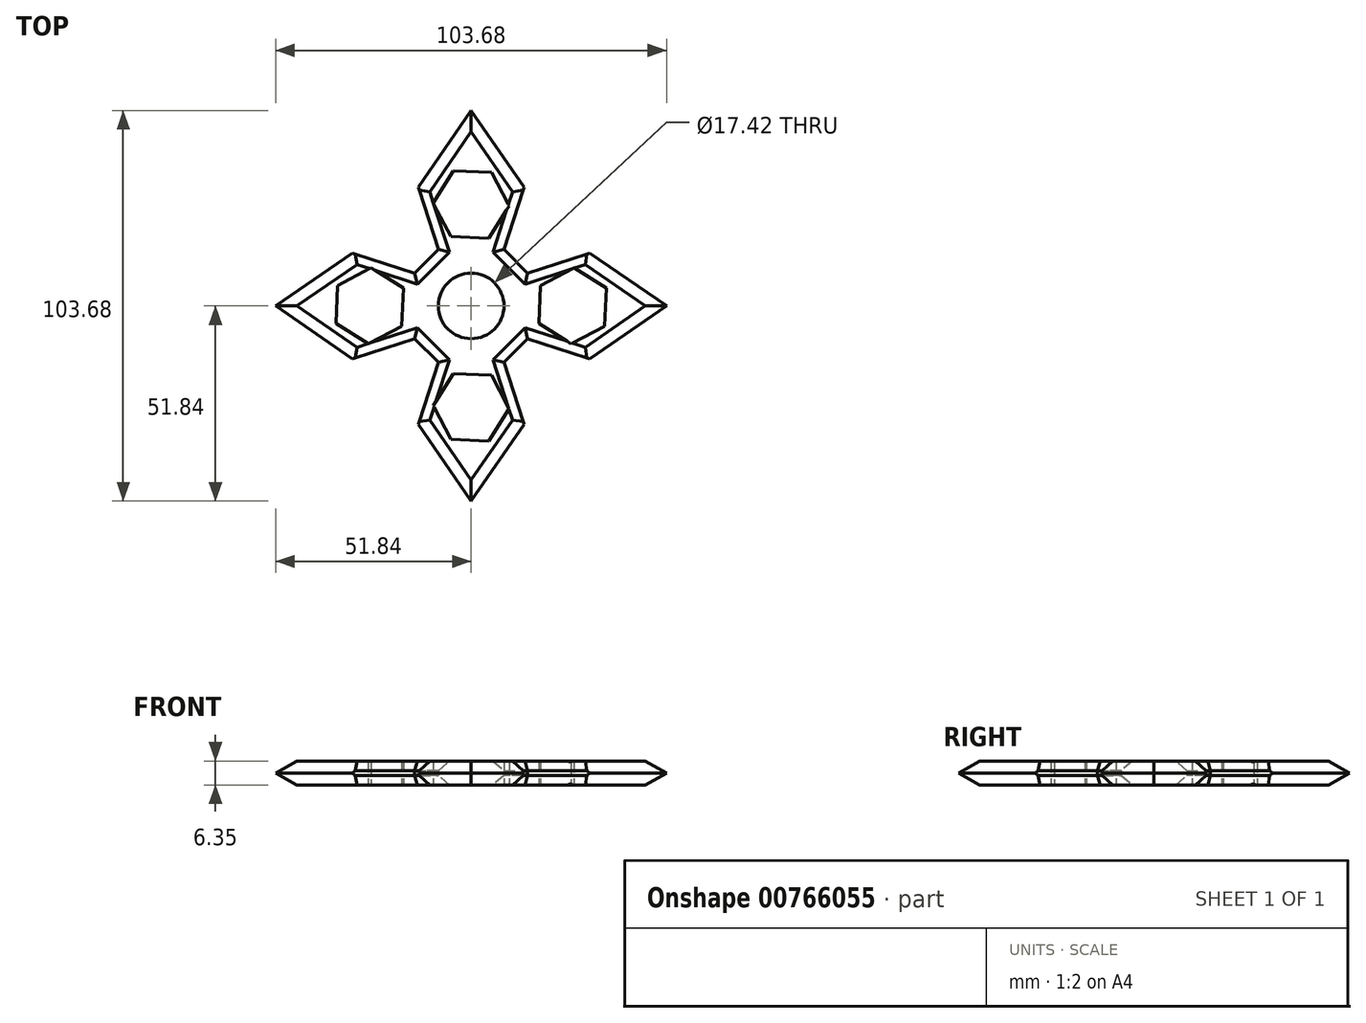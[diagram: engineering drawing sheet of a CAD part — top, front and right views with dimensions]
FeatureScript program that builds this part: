
annotation { "Feature Type Name" : "Feature", "Feature Type Description" : "" }
export const myFeature = defineFeature(function(context is Context, id is Id, definition is map)
    precondition{}
    {
        {
            var Q0;
            Q0=qCreatedBy(makeId("Top.planeOp"),FACE);
            var sketch = newSketch(context, id + "F0", { "sketchPlane" : qUnion([Q0])});
            skCircle(sketch, "E0", {"center": v(0, 0) * mm, "radius": 8.71 * mm});
            skCircle(sketch, "E1", {"center": v(0, 0) * mm, "radius": 14.29 * mm});
            skCircle(sketch, "E2.cCircle", {"center": v(0, 26.92) * mm, "radius": 8.73 * mm, "construction": true});
            skLineSegment(sketch, "E2.0", {"start": v(10.07, 26.52) * mm, "end": v(4.7, 18) * mm});
            skLineSegment(sketch, "E2.1", {"start": v(4.7, 18) * mm, "end": v(-5.38, 18.4) * mm});
            skLineSegment(sketch, "E2.2", {"start": v(-5.38, 18.4) * mm, "end": v(-10.07, 27.32) * mm});
            skLineSegment(sketch, "E2.3", {"start": v(-10.07, 27.32) * mm, "end": v(-4.7, 35.85) * mm});
            skLineSegment(sketch, "E2.4", {"start": v(-4.7, 35.85) * mm, "end": v(5.38, 35.45) * mm});
            skLineSegment(sketch, "E2.5", {"start": v(5.38, 35.45) * mm, "end": v(10.07, 26.52) * mm});
            skPoint(sketch, "E2.0.midPoint", {"position": v(7.38, 22.26) * mm});
            skCircle(sketch, "E3.cCircle", {"center": v(0, 26.92) * mm, "radius": 11.94 * mm, "construction": true});
            skLineSegment(sketch, "E3.0", {"start": v(8.67, 14.99) * mm, "end": v(-8.67, 14.99) * mm});
            skLineSegment(sketch, "E3.1", {"start": v(-8.67, 14.99) * mm, "end": v(-14.03, 31.48) * mm});
            skLineSegment(sketch, "E3.2", {"start": v(-14.03, 31.48) * mm, "end": v(0, 41.68) * mm});
            skLineSegment(sketch, "E3.3", {"start": v(0, 41.68) * mm, "end": v(14.03, 31.48) * mm});
            skLineSegment(sketch, "E3.4", {"start": v(14.03, 31.48) * mm, "end": v(8.67, 14.99) * mm});
            skPoint(sketch, "E3.0.midPoint", {"position": v(0, 14.99) * mm});
            skLineSegment(sketch, "E4", {"start": v(-14.03, 31.48) * mm, "end": v(0, 51.84) * mm});
            skLineSegment(sketch, "E5", {"start": v(0, 51.84) * mm, "end": v(14.03, 31.48) * mm});
            skPoint(sketch, "E6.1.0", {"position": v(-22.26, 7.38) * mm});
            skCircle(sketch, "E6.1.1", {"center": v(-26.92, 0) * mm, "radius": 8.73 * mm, "construction": true});
            skLineSegment(sketch, "E6.1.2", {"start": v(-14.99, 8.67) * mm, "end": v(-14.99, -8.67) * mm});
            skCircle(sketch, "E6.1.3", {"center": v(-26.92, 0) * mm, "radius": 11.94 * mm, "construction": true});
            skLineSegment(sketch, "E6.1.4", {"start": v(-35.45, 5.38) * mm, "end": v(-26.52, 10.07) * mm});
            skLineSegment(sketch, "E6.1.5", {"start": v(-41.68, 0) * mm, "end": v(-31.48, 14.03) * mm});
            skLineSegment(sketch, "E6.1.6", {"start": v(-31.48, -14.03) * mm, "end": v(-41.68, 0) * mm});
            skLineSegment(sketch, "E6.1.7", {"start": v(-31.48, 14.03) * mm, "end": v(-14.99, 8.67) * mm});
            skPoint(sketch, "E6.1.8", {"position": v(-14.99, 0) * mm});
            skLineSegment(sketch, "E6.1.9", {"start": v(-31.48, -14.03) * mm, "end": v(-51.84, 0) * mm});
            skLineSegment(sketch, "E6.1.10", {"start": v(-14.99, -8.67) * mm, "end": v(-31.48, -14.03) * mm});
            skLineSegment(sketch, "E6.1.11", {"start": v(-51.84, 0) * mm, "end": v(-31.48, 14.03) * mm});
            skLineSegment(sketch, "E6.1.12", {"start": v(-18.4, -5.38) * mm, "end": v(-27.32, -10.07) * mm});
            skLineSegment(sketch, "E6.1.13", {"start": v(-27.32, -10.07) * mm, "end": v(-35.85, -4.7) * mm});
            skLineSegment(sketch, "E6.1.14", {"start": v(-35.85, -4.7) * mm, "end": v(-35.45, 5.38) * mm});
            skLineSegment(sketch, "E6.1.15", {"start": v(-18, 4.7) * mm, "end": v(-18.4, -5.38) * mm});
            skLineSegment(sketch, "E6.1.16", {"start": v(-26.52, 10.07) * mm, "end": v(-18, 4.7) * mm});
            skPoint(sketch, "E6.2.0", {"position": v(-7.38, -22.26) * mm});
            skCircle(sketch, "E6.2.1", {"center": v(0, -26.92) * mm, "radius": 8.73 * mm, "construction": true});
            skLineSegment(sketch, "E6.2.2", {"start": v(-8.67, -14.99) * mm, "end": v(8.67, -14.99) * mm});
            skCircle(sketch, "E6.2.3", {"center": v(0, -26.92) * mm, "radius": 11.94 * mm, "construction": true});
            skLineSegment(sketch, "E6.2.4", {"start": v(-5.38, -35.45) * mm, "end": v(-10.07, -26.52) * mm});
            skLineSegment(sketch, "E6.2.5", {"start": v(0, -41.68) * mm, "end": v(-14.03, -31.48) * mm});
            skLineSegment(sketch, "E6.2.6", {"start": v(14.03, -31.48) * mm, "end": v(0, -41.68) * mm});
            skLineSegment(sketch, "E6.2.7", {"start": v(-14.03, -31.48) * mm, "end": v(-8.67, -14.99) * mm});
            skPoint(sketch, "E6.2.8", {"position": v(0, -14.99) * mm});
            skLineSegment(sketch, "E6.2.9", {"start": v(14.03, -31.48) * mm, "end": v(0, -51.84) * mm});
            skLineSegment(sketch, "E6.2.10", {"start": v(8.67, -14.99) * mm, "end": v(14.03, -31.48) * mm});
            skLineSegment(sketch, "E6.2.11", {"start": v(0, -51.84) * mm, "end": v(-14.03, -31.48) * mm});
            skLineSegment(sketch, "E6.2.12", {"start": v(5.38, -18.4) * mm, "end": v(10.07, -27.32) * mm});
            skLineSegment(sketch, "E6.2.13", {"start": v(10.07, -27.32) * mm, "end": v(4.7, -35.85) * mm});
            skLineSegment(sketch, "E6.2.14", {"start": v(4.7, -35.85) * mm, "end": v(-5.38, -35.45) * mm});
            skLineSegment(sketch, "E6.2.15", {"start": v(-4.7, -18) * mm, "end": v(5.38, -18.4) * mm});
            skLineSegment(sketch, "E6.2.16", {"start": v(-10.07, -26.52) * mm, "end": v(-4.7, -18) * mm});
            skPoint(sketch, "E6.3.0", {"position": v(22.26, -7.38) * mm});
            skCircle(sketch, "E6.3.1", {"center": v(26.92, 0) * mm, "radius": 8.73 * mm, "construction": true});
            skLineSegment(sketch, "E6.3.2", {"start": v(14.99, -8.67) * mm, "end": v(14.99, 8.67) * mm});
            skCircle(sketch, "E6.3.3", {"center": v(26.92, 0) * mm, "radius": 11.94 * mm, "construction": true});
            skLineSegment(sketch, "E6.3.4", {"start": v(35.45, -5.38) * mm, "end": v(26.52, -10.07) * mm});
            skLineSegment(sketch, "E6.3.5", {"start": v(41.68, 0) * mm, "end": v(31.48, -14.03) * mm});
            skLineSegment(sketch, "E6.3.6", {"start": v(31.48, 14.03) * mm, "end": v(41.68, 0) * mm});
            skLineSegment(sketch, "E6.3.7", {"start": v(31.48, -14.03) * mm, "end": v(14.99, -8.67) * mm});
            skPoint(sketch, "E6.3.8", {"position": v(14.99, 0) * mm});
            skLineSegment(sketch, "E6.3.9", {"start": v(31.48, 14.03) * mm, "end": v(51.84, 0) * mm});
            skLineSegment(sketch, "E6.3.10", {"start": v(14.99, 8.67) * mm, "end": v(31.48, 14.03) * mm});
            skLineSegment(sketch, "E6.3.11", {"start": v(51.84, 0) * mm, "end": v(31.48, -14.03) * mm});
            skLineSegment(sketch, "E6.3.12", {"start": v(18.4, 5.38) * mm, "end": v(27.32, 10.07) * mm});
            skLineSegment(sketch, "E6.3.13", {"start": v(27.32, 10.07) * mm, "end": v(35.85, 4.7) * mm});
            skLineSegment(sketch, "E6.3.14", {"start": v(35.85, 4.7) * mm, "end": v(35.45, -5.38) * mm});
            skLineSegment(sketch, "E6.3.15", {"start": v(18, -4.7) * mm, "end": v(18.4, 5.38) * mm});
            skLineSegment(sketch, "E6.3.16", {"start": v(26.52, -10.07) * mm, "end": v(18, -4.7) * mm});
            skLineSegment(sketch, "E7", {"start": v(-8.67, 14.99) * mm, "end": v(-14.99, 8.67) * mm});
            skLineSegment(sketch, "E8", {"start": v(-14.99, -8.67) * mm, "end": v(-8.67, -14.99) * mm});
            skLineSegment(sketch, "E9", {"start": v(8.67, -14.99) * mm, "end": v(14.99, -8.67) * mm});
            skLineSegment(sketch, "E10", {"start": v(14.99, 8.67) * mm, "end": v(8.67, 14.99) * mm});
            skSolve(sketch);
        }
        {
            var Q0;
            Q0=makeQuery(id+"F0.imprint","IMPRINT",FACE,{"disambiguationData":[TD([[makeQuery(id+"F0.imprint","IMPRINT",EDGE,{"derivedFrom":sQuery(id+"F0.wireOp",EDGE,"E6.1.5")}),1.0]])]});
            var Q1;
            Q1=makeQuery(id+"F0.imprint","IMPRINT",FACE,{"disambiguationData":[TD([[makeQuery(id+"F0.imprint","IMPRINT",EDGE,{"derivedFrom":sQuery(id+"F0.wireOp",EDGE,"E6.1.2")}),-1.0]])]});
            var Q2;
            Q2=makeQuery(id+"F0.imprint","IMPRINT",FACE,{"disambiguationData":[TD([[makeQuery(id+"F0.imprint","IMPRINT",EDGE,{"derivedFrom":sQuery(id+"F0.wireOp",EDGE,"E0")}),-1.0]])]});
            var Q3;
            Q3=makeQuery(id+"F0.imprint","IMPRINT",FACE,{"disambiguationData":[TD([[makeQuery(id+"F0.imprint","IMPRINT",EDGE,{"derivedFrom":sQuery(id+"F0.wireOp",EDGE,"E1")}),-1.0]])]});
            var Q4;
            Q4=makeQuery(id+"F0.imprint","IMPRINT",FACE,{"disambiguationData":[TD([[makeQuery(id+"F0.imprint","IMPRINT",EDGE,{"derivedFrom":sQuery(id+"F0.wireOp",EDGE,"E6.2.2")}),-1.0]])]});
            var Q5;
            Q5=makeQuery(id+"F0.imprint","IMPRINT",FACE,{"disambiguationData":[TD([[makeQuery(id+"F0.imprint","IMPRINT",EDGE,{"derivedFrom":sQuery(id+"F0.wireOp",EDGE,"E6.2.5")}),1.0]])]});
            var Q6;
            Q6=makeQuery(id+"F0.imprint","IMPRINT",FACE,{"disambiguationData":[TD([[makeQuery(id+"F0.imprint","IMPRINT",EDGE,{"derivedFrom":sQuery(id+"F0.wireOp",EDGE,"E6.3.5")}),1.0]])]});
            var Q7;
            Q7=makeQuery(id+"F0.imprint","IMPRINT",FACE,{"disambiguationData":[TD([[makeQuery(id+"F0.imprint","IMPRINT",EDGE,{"derivedFrom":sQuery(id+"F0.wireOp",EDGE,"E6.3.2")}),-1.0]])]});
            var Q8;
            Q8=makeQuery(id+"F0.imprint","IMPRINT",FACE,{"disambiguationData":[TD([[makeQuery(id+"F0.imprint","IMPRINT",EDGE,{"derivedFrom":sQuery(id+"F0.wireOp",EDGE,"E2.0")}),1.0]])]});
            var Q9;
            Q9=makeQuery(id+"F0.imprint","IMPRINT",FACE,{"disambiguationData":[TD([[makeQuery(id+"F0.imprint","IMPRINT",EDGE,{"derivedFrom":sQuery(id+"F0.wireOp",EDGE,"E3.2")}),1.0]])]});
            extrude(context, id + "F1", {"entities" : qUnion([Q0, Q1, Q2, Q3, Q4, Q5, Q6, Q7, Q8, Q9]), "depth" : 6.35 * mm, "offsetDistance" : 25.4 * mm});
        }
        {
            var Q0;
            Q0=makeQuery(id+"F1.opExtrude","CAP_EDGE",EDGE,{"disambiguationData":[OSD([sQuery(id+"F0.wireOp",EDGE,"E9")])],"isStart":false});
            var Q1;
            Q1=makeQuery(id+"F1.opExtrude","CAP_EDGE",EDGE,{"disambiguationData":[OSD([sQuery(id+"F0.wireOp",EDGE,"E9")])],"isStart":true});
            var Q2;
            Q2=makeQuery(id+"F1.opExtrude","CAP_EDGE",EDGE,{"disambiguationData":[OSD([sQuery(id+"F0.wireOp",EDGE,"E6.2.10")])],"isStart":true});
            var Q3;
            Q3=makeQuery(id+"F1.opExtrude","CAP_EDGE",EDGE,{"disambiguationData":[OSD([sQuery(id+"F0.wireOp",EDGE,"E6.2.10")])],"isStart":false});
            var Q4;
            Q4=makeQuery(id+"F1.opExtrude","CAP_EDGE",EDGE,{"disambiguationData":[OSD([sQuery(id+"F0.wireOp",EDGE,"E6.3.7")])],"isStart":true});
            var Q5;
            Q5=makeQuery(id+"F1.opExtrude","CAP_EDGE",EDGE,{"disambiguationData":[OSD([sQuery(id+"F0.wireOp",EDGE,"E6.3.7")])],"isStart":false});
            var Q6;
            Q6=makeQuery(id+"F1.opExtrude","CAP_EDGE",EDGE,{"disambiguationData":[OSD([sQuery(id+"F0.wireOp",EDGE,"E6.3.10")])],"isStart":false});
            var Q7;
            Q7=makeQuery(id+"F1.opExtrude","CAP_EDGE",EDGE,{"disambiguationData":[OSD([sQuery(id+"F0.wireOp",EDGE,"E6.3.10")])],"isStart":true});
            var Q8;
            Q8=makeQuery(id+"F1.opExtrude","CAP_EDGE",EDGE,{"disambiguationData":[OSD([sQuery(id+"F0.wireOp",EDGE,"E10")])],"isStart":true});
            var Q9;
            Q9=makeQuery(id+"F1.opExtrude","CAP_EDGE",EDGE,{"disambiguationData":[OSD([sQuery(id+"F0.wireOp",EDGE,"E10")])],"isStart":false});
            var Q10;
            Q10=makeQuery(id+"F1.opExtrude","CAP_EDGE",EDGE,{"disambiguationData":[OSD([sQuery(id+"F0.wireOp",EDGE,"E3.4")])],"isStart":true});
            var Q11;
            Q11=makeQuery(id+"F1.opExtrude","CAP_EDGE",EDGE,{"disambiguationData":[OSD([sQuery(id+"F0.wireOp",EDGE,"E3.4")])],"isStart":false});
            var Q12;
            Q12=makeQuery(id+"F1.opExtrude","CAP_EDGE",EDGE,{"disambiguationData":[OSD([sQuery(id+"F0.wireOp",EDGE,"E3.1")])],"isStart":false});
            var Q13;
            Q13=makeQuery(id+"F1.opExtrude","CAP_EDGE",EDGE,{"disambiguationData":[OSD([sQuery(id+"F0.wireOp",EDGE,"E3.1")])],"isStart":true});
            var Q14;
            Q14=makeQuery(id+"F1.opExtrude","CAP_EDGE",EDGE,{"disambiguationData":[OSD([sQuery(id+"F0.wireOp",EDGE,"E7")])],"isStart":false});
            var Q15;
            Q15=makeQuery(id+"F1.opExtrude","CAP_EDGE",EDGE,{"disambiguationData":[OSD([sQuery(id+"F0.wireOp",EDGE,"E7")])],"isStart":true});
            var Q16;
            Q16=makeQuery(id+"F1.opExtrude","CAP_EDGE",EDGE,{"disambiguationData":[OSD([sQuery(id+"F0.wireOp",EDGE,"E6.1.7")])],"isStart":true});
            var Q17;
            Q17=makeQuery(id+"F1.opExtrude","CAP_EDGE",EDGE,{"disambiguationData":[OSD([sQuery(id+"F0.wireOp",EDGE,"E6.1.7")])],"isStart":false});
            var Q18;
            Q18=makeQuery(id+"F1.opExtrude","CAP_EDGE",EDGE,{"disambiguationData":[OSD([sQuery(id+"F0.wireOp",EDGE,"E6.1.10")])],"isStart":false});
            var Q19;
            Q19=makeQuery(id+"F1.opExtrude","CAP_EDGE",EDGE,{"disambiguationData":[OSD([sQuery(id+"F0.wireOp",EDGE,"E6.1.10")])],"isStart":true});
            var Q20;
            Q20=makeQuery(id+"F1.opExtrude","CAP_EDGE",EDGE,{"disambiguationData":[OSD([sQuery(id+"F0.wireOp",EDGE,"E8")])],"isStart":false});
            var Q21;
            Q21=makeQuery(id+"F1.opExtrude","CAP_EDGE",EDGE,{"disambiguationData":[OSD([sQuery(id+"F0.wireOp",EDGE,"E8")])],"isStart":true});
            var Q22;
            Q22=makeQuery(id+"F1.opExtrude","CAP_EDGE",EDGE,{"disambiguationData":[OSD([sQuery(id+"F0.wireOp",EDGE,"E6.2.7")])],"isStart":false});
            var Q23;
            Q23=makeQuery(id+"F1.opExtrude","CAP_EDGE",EDGE,{"disambiguationData":[OSD([sQuery(id+"F0.wireOp",EDGE,"E6.2.7")])],"isStart":true});
            chamfer(context, id + "F2", {"entities" : qUnion([Q0, Q1, Q2, Q3, Q4, Q5, Q6, Q7, Q8, Q9, Q10, Q11, Q12, Q13, Q14, Q15, Q16, Q17, Q18, Q19, Q20, Q21, Q22, Q23]), "width" : 2.54 * mm, "tangentPropagation" : true});
        }
        {
            var Q0;
            Q0=makeQuery(id+"F1.opExtrude","CAP_EDGE",EDGE,{"disambiguationData":[OSD([sQuery(id+"F0.wireOp",EDGE,"E6.2.9")])],"isStart":true});
            var Q1;
            Q1=makeQuery(id+"F1.opExtrude","CAP_EDGE",EDGE,{"disambiguationData":[OSD([sQuery(id+"F0.wireOp",EDGE,"E6.2.9")])],"isStart":false});
            var Q2;
            Q2=makeQuery(id+"F1.opExtrude","CAP_EDGE",EDGE,{"disambiguationData":[OSD([sQuery(id+"F0.wireOp",EDGE,"E6.2.11")])],"isStart":true});
            var Q3;
            Q3=makeQuery(id+"F1.opExtrude","CAP_EDGE",EDGE,{"disambiguationData":[OSD([sQuery(id+"F0.wireOp",EDGE,"E6.2.11")])],"isStart":false});
            var Q4;
            Q4=makeQuery(id+"F1.opExtrude","CAP_EDGE",EDGE,{"disambiguationData":[OSD([sQuery(id+"F0.wireOp",EDGE,"E6.1.9")])],"isStart":true});
            var Q5;
            Q5=makeQuery(id+"F1.opExtrude","CAP_EDGE",EDGE,{"disambiguationData":[OSD([sQuery(id+"F0.wireOp",EDGE,"E6.1.9")])],"isStart":false});
            var Q6;
            Q6=makeQuery(id+"F1.opExtrude","CAP_EDGE",EDGE,{"disambiguationData":[OSD([sQuery(id+"F0.wireOp",EDGE,"E6.1.11")])],"isStart":true});
            var Q7;
            Q7=makeQuery(id+"F1.opExtrude","CAP_EDGE",EDGE,{"disambiguationData":[OSD([sQuery(id+"F0.wireOp",EDGE,"E6.1.11")])],"isStart":false});
            var Q8;
            Q8=makeQuery(id+"F1.opExtrude","CAP_EDGE",EDGE,{"disambiguationData":[OSD([sQuery(id+"F0.wireOp",EDGE,"E4")])],"isStart":true});
            var Q9;
            Q9=makeQuery(id+"F1.opExtrude","CAP_EDGE",EDGE,{"disambiguationData":[OSD([sQuery(id+"F0.wireOp",EDGE,"E4")])],"isStart":false});
            var Q10;
            Q10=makeQuery(id+"F1.opExtrude","CAP_EDGE",EDGE,{"disambiguationData":[OSD([sQuery(id+"F0.wireOp",EDGE,"E5")])],"isStart":true});
            var Q11;
            Q11=makeQuery(id+"F1.opExtrude","CAP_EDGE",EDGE,{"disambiguationData":[OSD([sQuery(id+"F0.wireOp",EDGE,"E5")])],"isStart":false});
            var Q12;
            Q12=makeQuery(id+"F1.opExtrude","CAP_EDGE",EDGE,{"disambiguationData":[OSD([sQuery(id+"F0.wireOp",EDGE,"E6.3.9")])],"isStart":true});
            var Q13;
            Q13=makeQuery(id+"F1.opExtrude","CAP_EDGE",EDGE,{"disambiguationData":[OSD([sQuery(id+"F0.wireOp",EDGE,"E6.3.9")])],"isStart":false});
            var Q14;
            Q14=makeQuery(id+"F1.opExtrude","CAP_EDGE",EDGE,{"disambiguationData":[OSD([sQuery(id+"F0.wireOp",EDGE,"E6.3.11")])],"isStart":true});
            var Q15;
            Q15=makeQuery(id+"F1.opExtrude","CAP_EDGE",EDGE,{"disambiguationData":[OSD([sQuery(id+"F0.wireOp",EDGE,"E6.3.11")])],"isStart":false});
            chamfer(context, id + "F3", {"entities" : qUnion([Q0, Q1, Q2, Q3, Q4, Q5, Q6, Q7, Q8, Q9, Q10, Q11, Q12, Q13, Q14, Q15]), "width" : 3.17 * mm, "tangentPropagation" : true});
        }
    });
